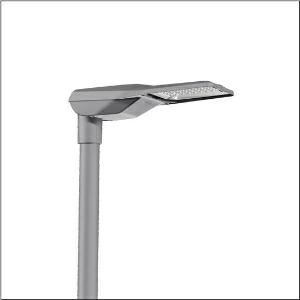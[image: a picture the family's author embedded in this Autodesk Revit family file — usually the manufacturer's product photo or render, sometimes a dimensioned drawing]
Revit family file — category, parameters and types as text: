
# Revit family: streetlight_sl_21_iq_mini___st1_0a_5xe2d41d08jb_acb7
name_source: partatom
category: Lighting Fixtures
units: mm (PartAtom-declared; Revit-internal decimal feet)

## family parameters
Cut with Voids When Loaded = No
Host = Face
Light Source = No
Part Type = Normal
Room Calculation Point = No
Round Connector Dimension = Use Diameter
Shared = No

## types (1)
- --- (1 x LED, 11290 lm, 71.6 W, 4000K)
    Apparent Load = 72 VA
    CIE Flux Codes = 40 73 97 100 100
    Color Rendering = 70
    Color Temperature = 4000K
    Default Elevation = 1800 mm
    Description = Streetlight SL 21 iQ mini, mast luminaire, primary light control with lens, of PMMA, primary optical cover: cover, of toughened safety glass, transparent, light distribution: ST1.0a, light emission: direct distribution, primary light characteristic: asymmetric, installation type: post-top, side-entry, LED, High Power LED, rated luminous flux: 11.290lm, luminous efficacy: 158lm/W, light colour: 740, colour temperature: 4000K, control gear: iQ-Comfort, control: Auto-Match, Temp-Guard, Lumen-Switch, Night-Set, Smart-Wire, Light-Fading, Desk-Remote (wireless, voltage-free reading and setting of iQ features in the workshop via application-optimized NFC function/RFID function), optimised constant luminous flux control (CLO 2.0), pre-setting: linear dimming characteristic, mains connection: 220..240V, AC, 50/60Hz, start of lifetime: 72W, end of service life: 75W, reduction: 33W, luminaire housing, of diecast aluminium, powder-coated, SITECO metallic grey (DB 702S), corrosivity category C5 high according to DIN EN ISO 12944, please order mast flange separately, inclination adjustable: 0°, 5°, 10°, 15°, sealing non-destructively replaceable, multi-level sealing system, length: 628mm, width: 235mm, height: 110mm, mast flange for spigot size: 42mm (side-entry): 5XC10008XM4, 60/48mm (side-entry/post-top): 5XC10108XM2, 76/60mm (side-entry/post-top): 5XC10108XM1, mounting height: 4..8m, protection rating (complete): IP66, insulation class (complete): insulation class II (safety insulation), certification: CE, ENEC, ENEC+, VDE, impact resistance: IK10, permissible operating ambient temperature for outdoor applications: -40..+50°C, standard-compliant lighting for roads and squares, packaging unit: 1 piece

Light Distribution: ST1.0a
    Height = 110 mm
    Lamp = 1 x LED
    Lamp Light Flux = 11290 lm
    Lamp Power = 71.6 W
    Lamp count = 1
    Length = 625 mm
    Luminous efficacy = 158 lm/W
    Manufacturer = Siteco
    ModVariant = No
    Model = 5XE2D41D08JB
    Mounting Place = Pole
    Mounting Type = Pole top
    Number of Poles = 1
    OnlyDefault = Yes
    Power Factor = 1
    Product Name = Streetlight SL 21 iQ mini | ST1.0a
    Product group = mast luminaire | pylon top
    ProductGroupID = 6100
    Protection Class = Protection class II
    Protection Degree = IP 66
    RLX_Detail_Level = 1
    RLX_Emergency_Light_Flux = 0 lm
    RLX_Emergency_Type = 0
    RLX_Emergency_Type_DB = No
    RlxData = <blob elided: 26369 chars, md5=ec2266e9>
    Socket = socket
    Standby Power = 0 W
    System Light Flux = 11290 lm
    System Power = 72 W
    Type Comments = factory setting: luminous flux: 100 % | dim-lin: 254 | 746 mA
    Type Image = l_1003519.jpg
    URL = http://relux.com
    VarID = @adj_172157
    Voltage = 0 V
    Weight = 0.00 kg
    Width = 234 mm

## geometry (parser evidence)
native form markers: Blend x4, Sweep x10
no freeform markers — native parametric forms only
